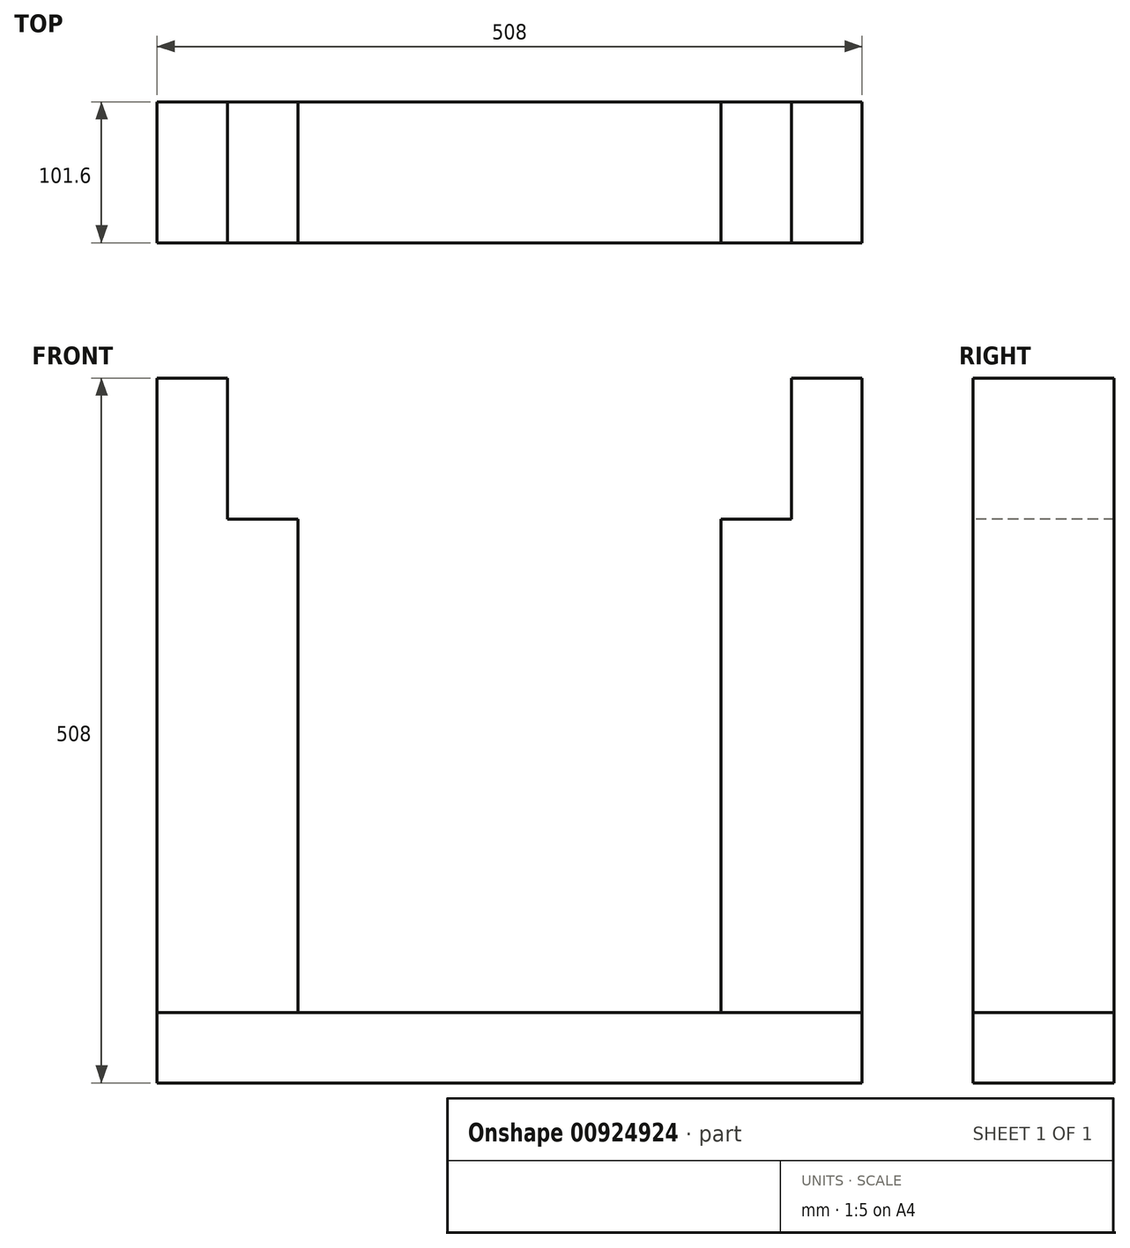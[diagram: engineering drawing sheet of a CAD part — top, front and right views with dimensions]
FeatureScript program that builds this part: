
annotation { "Feature Type Name" : "Feature", "Feature Type Description" : "" }
export const myFeature = defineFeature(function(context is Context, id is Id, definition is map)
    precondition{}
    {
        {
            var Q0;
            Q0=qCreatedBy(makeId("Top.planeOp"),FACE);
            var sketch = newSketch(context, id + "F0", { "sketchPlane" : qUnion([Q0])});
            skLineSegment(sketch, "E0.bottom", {"start": v(0, 101.6) * mm, "end": v(50.8, 101.6) * mm});
            skLineSegment(sketch, "E0.top", {"start": v(0, 0) * mm, "end": v(50.8, 0) * mm});
            skLineSegment(sketch, "E0.left", {"start": v(0, 101.6) * mm, "end": v(0, 0) * mm});
            skLineSegment(sketch, "E0.right", {"start": v(50.8, 101.6) * mm, "end": v(50.8, 0) * mm});
            skSolve(sketch);
        }
        {
            var Q0;
            Q0=makeQuery(id+"F0.imprint","IMPRINT",FACE,{"disambiguationData":[TD([[makeQuery(id+"F0.imprint","IMPRINT",EDGE,{"derivedFrom":sQuery(id+"F0.wireOp",EDGE,"E0.bottom")}),-1.0]])]});
            extrude(context, id + "F1", {"entities" : qUnion([Q0]), "depth" : 457.2 * mm, "offsetDistance" : 25.4 * mm});
        }
        {
            var Q0;
            Q0=qCreatedBy(makeId("Top.planeOp"),FACE);
            var sketch = newSketch(context, id + "F2", { "sketchPlane" : qUnion([Q0])});
            skLineSegment(sketch, "E1.bottom", {"start": v(50.8, 101.6) * mm, "end": v(101.6, 101.6) * mm});
            skLineSegment(sketch, "E1.top", {"start": v(50.8, 0) * mm, "end": v(101.6, 0) * mm});
            skLineSegment(sketch, "E1.left", {"start": v(50.8, 101.6) * mm, "end": v(50.8, 0) * mm});
            skLineSegment(sketch, "E1.right", {"start": v(101.6, 101.6) * mm, "end": v(101.6, 0) * mm});
            skSolve(sketch);
        }
        {
            var Q0;
            Q0 = qSketchRegion(id + "F2", true);
            extrude(context, id + "F3", {"entities" : qUnion([Q0]), "operationType" : NewBodyOperationType.ADD, "depth" : 355.6 * mm, "offsetDistance" : 25.4 * mm});
        }
        {
            var Q0;
            Q0=makeQuery(id+"F3.opExtrude","SWEPT_FACE",FACE,{"disambiguationData":[OSD([sQuery(id+"F2.wireOp",EDGE,"E1.right")])]});
            cPlane(context, id + "F4", {"entities" : qUnion([Q0]), "cplaneType" : CPlaneType.OFFSET, "offset" : 152.4 * mm, "width" : 152.4 * mm, "height" : 152.4 * mm});
        }
        {
            var Q0;
            Q0=makeQuery(id+"F1.opExtrude","SWEPT_BODY",BODY,{"disambiguationData":[OSD([sQuery(id+"F0.wireOp",EDGE,"E0.bottom"),sQuery(id+"F0.wireOp",EDGE,"E0.top"),sQuery(id+"F0.wireOp",EDGE,"E0.left"),sQuery(id+"F0.wireOp",EDGE,"E0.right")])]});
            var Q1;
            Q1=qCreatedBy(id+"F4.planeOp",FACE);
            mirror(context, id + "F5", {"entities" : qUnion([Q0]), "mirrorPlane" : qUnion([Q1])});
        }
        {
            var Q0;
            Q0=qCreatedBy(makeId("Top.planeOp"),FACE);
            var sketch = newSketch(context, id + "F6", { "sketchPlane" : qUnion([Q0])});
            skLineSegment(sketch, "E2.bottom", {"start": v(0, 0) * mm, "end": v(508, 0) * mm});
            skLineSegment(sketch, "E2.top", {"start": v(0, 101.6) * mm, "end": v(508, 101.6) * mm});
            skLineSegment(sketch, "E2.left", {"start": v(0, 0) * mm, "end": v(0, 101.6) * mm});
            skLineSegment(sketch, "E2.right", {"start": v(508, 0) * mm, "end": v(508, 101.6) * mm});
            skSolve(sketch);
        }
        {
            var Q0;
            Q0 = qSketchRegion(id + "F6", true);
            extrude(context, id + "F7", {"entities" : qUnion([Q0]), "oppositeDirection" : true, "depth" : 50.8 * mm, "offsetDistance" : 25.4 * mm});
        }
    });
